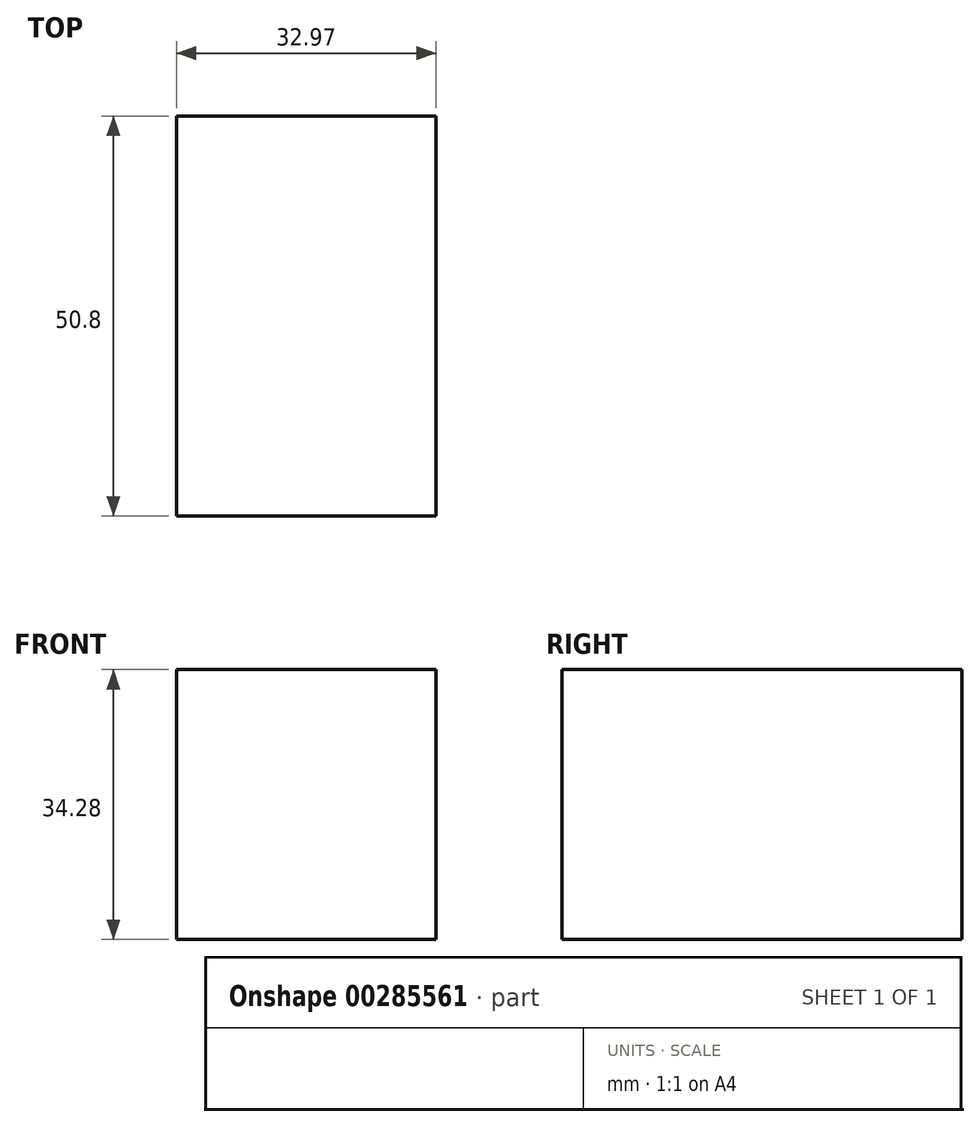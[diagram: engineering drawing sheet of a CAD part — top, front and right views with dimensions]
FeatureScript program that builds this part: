
annotation { "Feature Type Name" : "Feature", "Feature Type Description" : "" }
export const myFeature = defineFeature(function(context is Context, id is Id, definition is map)
    precondition{}
    {
        {
            var Q0;
            Q0=qCreatedBy(makeId("Front.planeOp"),FACE);
            var sketch = newSketch(context, id + "F0", { "sketchPlane" : qUnion([Q0])});
            skLineSegment(sketch, "E0.bottom", {"start": v(-32.97, 34.28) * mm, "end": v(0, 34.28) * mm});
            skLineSegment(sketch, "E0.top", {"start": v(-32.97, 0) * mm, "end": v(0, 0) * mm});
            skLineSegment(sketch, "E0.left", {"start": v(-32.97, 34.28) * mm, "end": v(-32.97, 0) * mm});
            skLineSegment(sketch, "E0.right", {"start": v(0, 34.28) * mm, "end": v(0, 0) * mm});
            skSolve(sketch);
        }
        {
            var Q0;
            Q0 = qSketchRegion(id + "F0", true);
            extrude(context, id + "F1", {"entities" : qUnion([Q0]), "depth" : 50.8 * mm});
        }
    });
